# Revit family: Mailboxes_4C-Salsbury_Industries-Rear_Load-5_Door_High_Units
name_source: partatom
category: Specialty Equipment
revit_build: Autodesk Revit 2016 (Build: 20150714_1515(x64)
units: mm (PartAtom-declared; Revit-internal decimal feet)

## family parameters
Always vertical = Yes
Cut with Voids When Loaded = No
Host = Wall
OmniClass Number = 23.40.90.14.11
OmniClass Title = Mail Boxes
Part Type = Normal
Room Calculation Point = No
Round Connector Dimension = Use Diameter
Shared = No

## types (7) — shared parameters
Assembly Code = C1030910
Assembly Description = Mailboxes
Back Enclosure Material = Aluminum - Salsbury Finish - Anodized
Bottom Back Plate = No
Depth = 17.025"
Height = 20.000"
Latch Distance = 8.963"
Latch Lock-Right Side = Yes
Lock Material = Stainless Steel - Salsbury Finish -  Polished
Manufacturer = Salsbury Industries
MasterFormat Number = 10 55 00
MasterFormat Title = Postal Specialties
OmniClass 23 Number = 23.40.90.14.11
OmniClass 23 Title = Mail Boxes
Top Back Plate = No
Type Comments = 4C Standard Horizontal Mailbox - Rear Loading
URL = www.mailboxes.com
Version = 3.0 (06/30/17)

## per-type parameters (varying)
| type | Description | Door Slot L1 | Door Slot L2 | Door Slot L3 | Door Slot L4 | Door Slot L5 | Door Slot R1 | Door Slot R2 | Door Slot R3 | Door Slot R4 | Door Slot R5 | Latch Alignment | Latch Lock-Left Side | Left Inside Wall | Right Inside Wall | Vertical Center Divider | Width |
| 3705D-08 RL | 5 Door High Unit:  8 MB1, OM2 | 3700 Series 4C Door Configurations : MB1 Door | 3700 Series 4C Door Configurations : MB1 Door w/ Divider | 3700 Series 4C Door Configurations : MB1 Door w/ Divider | 3700 Series 4C Door Configurations : MB1 Door w/ Divider | 3700 Series 4C Door Configurations : MB1 Door w/ Divider | 3700 Series 4C Door Configurations : MB1 Door | 3700 Series 4C Door Configurations : Empty | 3700 Series 4C OM2 Configuration : OM2-RL | 3700 Series 4C Door Configurations : MB1 Door w/ Divider | 3700 Series 4C Door Configurations : MB1 Door w/ Divider | 14.857" | Yes | Yes | Yes | Yes | 31.098" |
| 3705S-03 RL | 5 Door High Unit:  3 MB1, OM2 | 3700 Series 4C Door Configurations : Empty | 3700 Series 4C Door Configurations : Empty | 3700 Series 4C Door Configurations : Empty | 3700 Series 4C Door Configurations : Empty | 3700 Series 4C Door Configurations : Empty | 3700 Series 4C Door Configurations : MB1 Door | 3700 Series 4C Door Configurations : Empty | 3700 Series 4C OM2 Configuration : OM2-RL | 3700 Series 4C Door Configurations : MB1 Door w/ Divider | 3700 Series 4C Door Configurations : MB1 Door w/ Divider | 13.876" | No | No | No | No | 16.344" |
| 3705D-07 RL | 5 Door High Unit:  7 MB1, OM3 | 3700 Series 4C Door Configurations : MB1 Door | 3700 Series 4C Door Configurations : MB1 Door w/ Divider | 3700 Series 4C Door Configurations : MB1 Door w/ Divider | 3700 Series 4C Door Configurations : MB1 Door w/ Divider | 3700 Series 4C Door Configurations : MB1 Door w/ Divider | 3700 Series 4C Door Configurations : MB1 Door | 3700 Series 4C Door Configurations : Empty | 3700 Series 4C Door Configurations : Empty | 3700 Series 4C OM3 Configuration : OM3-RL | 3700 Series 4C Door Configurations : MB1 Door w/ Divider | 14.857" | Yes | Yes | Yes | Yes | 31.098" |
| 3705D-03 RL | 5 Door High Unit:  3 MB1, 1 PL5, OM2 | 3700 Series 4C Door Configurations : Empty | 3700 Series 4C Door Configurations : Empty | 3700 Series 4C Door Configurations : Empty | 3700 Series 4C Door Configurations : Empty | 3700 Series 4C Parcel Configurations : PL5 | 3700 Series 4C Door Configurations : MB1 Door | 3700 Series 4C Door Configurations : Empty | 3700 Series 4C OM2 Configuration : OM2-RL | 3700 Series 4C Door Configurations : MB1 Door w/ Divider | 3700 Series 4C Door Configurations : MB1 Door w/ Divider | 14.857" | Yes | Yes | Yes | Yes | 31.098" |
| 3705D-01 RL | 5 Door High Unit:  1 MB3, 1 PL5, OM2 | 3700 Series 4C Door Configurations : Empty | 3700 Series 4C Door Configurations : Empty | 3700 Series 4C Door Configurations : Empty | 3700 Series 4C Door Configurations : Empty | 3700 Series 4C Parcel Configurations : PL5 | 3700 Series 4C Door Configurations : Empty | 3700 Series 4C OM2 Configuration : OM2-RL | 3700 Series 4C Door Configurations : Empty | 3700 Series 4C Door Configurations : Empty | 3700 Series 4C Door Configurations : MB3 Door w/ Divider | 14.857" | Yes | Yes | Yes | Yes | 31.098" |
| 3705D-2P RL | 5 Door High Unit:  2 PL5 | 3700 Series 4C Door Configurations : Empty | 3700 Series 4C Door Configurations : Empty | 3700 Series 4C Door Configurations : Empty | 3700 Series 4C Door Configurations : Empty | 3700 Series 4C Parcel Configurations : PL5 | 3700 Series 4C Door Configurations : Empty | 3700 Series 4C Door Configurations : Empty | 3700 Series 4C Door Configurations : Empty | 3700 Series 4C Door Configurations : Empty | 3700 Series 4C Parcel Configurations : PL5 | 14.857" | Yes | Yes | Yes | Yes | 31.098" |
| 3705S-1P RL | 5 Door High Unit:  1 PL5 | 3700 Series 4C Door Configurations : Empty | 3700 Series 4C Door Configurations : Empty | 3700 Series 4C Door Configurations : Empty | 3700 Series 4C Door Configurations : Empty | 3700 Series 4C Door Configurations : Empty | 3700 Series 4C Door Configurations : Empty | 3700 Series 4C Door Configurations : Empty | 3700 Series 4C Door Configurations : Empty | 3700 Series 4C Door Configurations : Empty | 3700 Series 4C Parcel Configurations : PL5 | 13.876" | No | No | No | No | 16.344" |

note: column(s) folded — value = type name in every type: Model

## geometry (parser evidence)
native form markers: Blend x2, Sweep x21
no freeform markers — native parametric forms only
